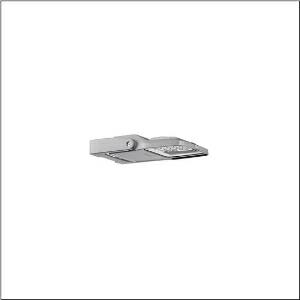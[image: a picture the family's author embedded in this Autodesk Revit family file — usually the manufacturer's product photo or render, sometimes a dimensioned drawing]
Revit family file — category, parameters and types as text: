
# Revit family: floodlight_fl_21_micro___pl61_5xa7762a2c2a_a5f7
name_source: partatom
category: Lighting Fixtures
units: mm (PartAtom-declared; Revit-internal decimal feet)

## family parameters
Cut with Voids When Loaded = No
Host = Face
Light Source = No
Part Type = Normal
Room Calculation Point = No
Round Connector Dimension = Use Diameter
Shared = No

## types (1)
- --- (1 x LED, 2910 lm, 23.1 W, 3000K)
    Apparent Load = 23 VA
    CIE Flux Codes = 33 65 98 100 100
    Color Rendering = 70
    Color Temperature = 3000K
    Default Elevation = 1800 mm
    Description = Floodlight FL 21 micro, floodlight, primary light control with lens, of PMMA, primary optical cover: protective disc, of toughened safety glass, transparent, light distribution: PL61, light emission: direct distribution, installation type: surface-mounted, LED, High Power LED, rated luminous flux: 2.910lm, luminous efficacy: 126lm/W, light colour: 730, colour temperature: 3000K, control gear: ECG iQ, control: Auto-Match, Temp-Guard, Night-Set, Smart-Wire, Desk-Remote (wireless, voltage-free reading and setting of iQ features in the workshop via application-optimized NFC function/RFID function), optimised constant luminous flux control (CLO 2.0), Street-Remote, with terminal, 6-pole, mains connection: 220..240V, AC, 50/60Hz, start of lifetime: 23W, end of lifetime: 24W, reduction: 11W, luminaire housing, of diecast aluminium, powder-coated, Siteco® metallic grey (DB 702S), corrosivity category C5 according to DIN EN ISO 12944, design bracket, of diecast aluminium, powder-coated, Siteco® metallic grey (DB 702S), protection rating (complete): IP66, insulation class (complete): insulation class II (safety insulation), certification: CE, protection symbol: D, impact resistance: IK07, permissible operating ambient temperature: -40..+40°C, permissible operating ambient temperature for outdoor applications: -40..+50°C, standard: DIN EN 12944, packaging unit: 1 piece

Light Distribution: PL61
    Height = 65 mm
    Lamp = 1 x LED
    Lamp Light Flux = 2910 lm
    Lamp Power = 23.1 W
    Lamp count = 1
    Length = 312 mm
    Luminous efficacy = 126 lm/W
    Manufacturer = Siteco
    ModVariant = No
    Model = 5XA7762A2C2A
    Number of Poles = 1
    OnlyDefault = Yes
    Power Factor = 1
    Product Name = Floodlight FL 21 micro | PL61
    Product group = floodlight | pylon top
    ProductGroupID = 6101
    Protection Class = Protection class II
    Protection Degree = IP 66
    RLX_Detail_Level = 1
    RlxData = <blob elided: 97693 chars, md5=031e810c>
    Socket = socket
    Standby Power = 0 W
    System Light Flux = 2910 lm
    System Power = 23 W
    Type Comments = factory setting: luminous flux: 100 % | dim-lin: 254 | 455 mA
    Type Image = l_1006878.jpg
    URL = http://relux.com
    VarID = @adj_115327
    Voltage = 0 V
    Weight = 0.00 kg
    Width = 230 mm

## geometry (parser evidence)
native form markers: Blend x4, Sweep x12
no freeform markers — native parametric forms only
